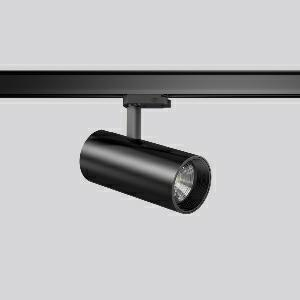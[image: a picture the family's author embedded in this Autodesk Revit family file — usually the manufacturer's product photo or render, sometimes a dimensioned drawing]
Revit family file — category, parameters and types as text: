
# Revit family: deecos_s_mini_742201_003_0c56
name_source: partatom
category: Lighting Fixtures
units: mm (PartAtom-declared; Revit-internal decimal feet)

## family parameters
Cut with Voids When Loaded = No
Host = Face
Light Source = No
Part Type = Normal
Room Calculation Point = No
Round Connector Dimension = Use Diameter
Shared = No

## types (1)
- DEECOS S mini (1 x LED Modul 930, 2250 lm, 3000)
    Apparent Load = 20 VA
    Approval mark = CE
    CIE Flux Codes = 80 99 100 100 100
    Color Rendering = 90
    Color Temperature = 3000
    Default Elevation = 1800 mm
    Description = Series: DEECOS S mini
LED surface-mounted projector in modern design with no visible cooling ribs. Housing: die-cast aluminium, powder-coated. Rotation range: 356°. Swivel range: 90°. Black plastic ring and recessed LED to prevent glare from the side. Optical assembly with lens made of plastic (polycarbonate) for the best homogeneous light distribution - can be changed without tools. Best colour rendering index Ra>90. With multi adaptor for 3-circuit tracks 230 V. Suitable for Track on ceiling, Wall track. High quality converter without flickering and stroboscopic effect. The following accessories can be mounted without use of tools: interchangeable lenses, decorative glasses, honeycomb louvre, clear and frosted diffusers, white interchangeable plastic ring. 
Colour: deep black, matt (RAL 9005)
Diameter: 87 mm
Height: 214 mm
Lamp: LED
Socket: without socket
Colour temperature: 3000K
Colour rendering index (CRI): 92
System power: 20 W
Rated luminous flux: 2250 lm
Luminous efficiency: 113 lm/W
Control gear: Regulated power supply
Protection class: I
Type of protection: IP 20
    Height = 214 mm
    Lamp = 1 x LED Modul 930
    Lamp Light Flux = 2250 lm
    Lamp count = 1
    Length = 87 mm
    Lifetime = 50000 h
    Luminous efficacy = 113 lm/W
    Manufacturer = RZB
    ModVariant = No
    Model = 742201.003
    Mounting Place = Ceiling
    Mounting Type = Rail mounted
    Number of Poles = 1
    OnlyDefault = Yes
    Power Factor = 1
    Product Name = DEECOS S mini
    Product group = Track mounted projectors
    ProductGroupID = 301
    Protection Class = Protection class I
    Protection Degree = IP 20
    RLX_Detail_Level = 1
    RLX_Emergency_Light_Flux = 0 lm
    RLX_Emergency_Type = 0
    RLX_Emergency_Type_DB = No
    RlxData = <blob elided: 39141 chars, md5=65dc4e66>
    Socket = socket
    Standby Power = 0 W
    System Light Flux = 2250 lm
    System Power = 20 W
    Type Comments = Product without accessories
    Type Image = 741930.003.jpg
    URL = http://relux.com
    VarID = ---
    Voltage = 230 V
    Voltage Range = 220-240 V
    Weight = 0.00 kg
    Width = 0 mm  [stored 0 ft]

note: [stored X ft] marks values corroborated as IEEE doubles in the binary element streams (Revit-internal decimal feet)

## geometry (parser evidence)
native form markers: Blend x4, Sweep x10
no freeform markers — native parametric forms only
